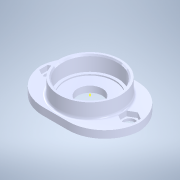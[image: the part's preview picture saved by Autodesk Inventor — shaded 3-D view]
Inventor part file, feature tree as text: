
AUTODESK INVENTOR PART (.ipt)
format: ipt  version: 2021 (Build 250183000, 183)  size: 201,216 bytes
history: mixed  units: in
note: dims shown in document units (in); Inventor stores cm internally (conversion verified against a paired STEP export)
features: sketch x6, extrude x4, delete_face x1, chamfer x1, fillet x1, other x1, imported_body x1
ambient origin geometry x8: Origin, YZ Plane, XZ Plane, XY Plane, X Axis, Y Axis, Z Axis, Center Point
bodies: Solid1 (imported_parasolid)
feature tree (15):
  extrude  "Extrusion1"  Depth=0.3937in TaperAngle=0.0deg
  extrude  "Extrusion2"  TaperAngle=0.0deg  [1 undecoded]
  sketch  "Sketch5"  dims[d8=0.9843in d9=0.3937in d10=0.0in]
  delete_face  "Delete Face1"
  extrude  "Extrusion4"  Depth=0.3937in TaperAngle=0.0deg
  extrude  "Extrusion5"  Depth=0.3937in TaperAngle=0.0deg
  chamfer  "Chamfer1"  Distance=0.0197in Angle=45.0deg
  sketch  "Sketch8"
  fillet  "Fillet1"  Radius=0.0394in
  sketch  "Sketch1"  dims[d0=0.7874in d1=0.3937in d2=0.0in]
  sketch  "Sketch2"  dims[d3=0.3937in d4=0.0in d5=0.0in]
  sketch  "Sketch6"  dims[d11=0.878in d12=0.3937in d13=0.0in d14=0.0197in d15=0.0787in d16=45.0deg d20=0.0394in]
  sketch  "Sketch7"
  other  "Cut-Extrude3"
  imported_body  NMx_Import_Brep_tag  [imported B-rep: ~6 faces, bbox_mm=None]
note: 1 required parameter value undecoded (feature->parameter linkage not recoverable at this tier; creation-order binding heuristic only, values carry confidence <= 0.55)
